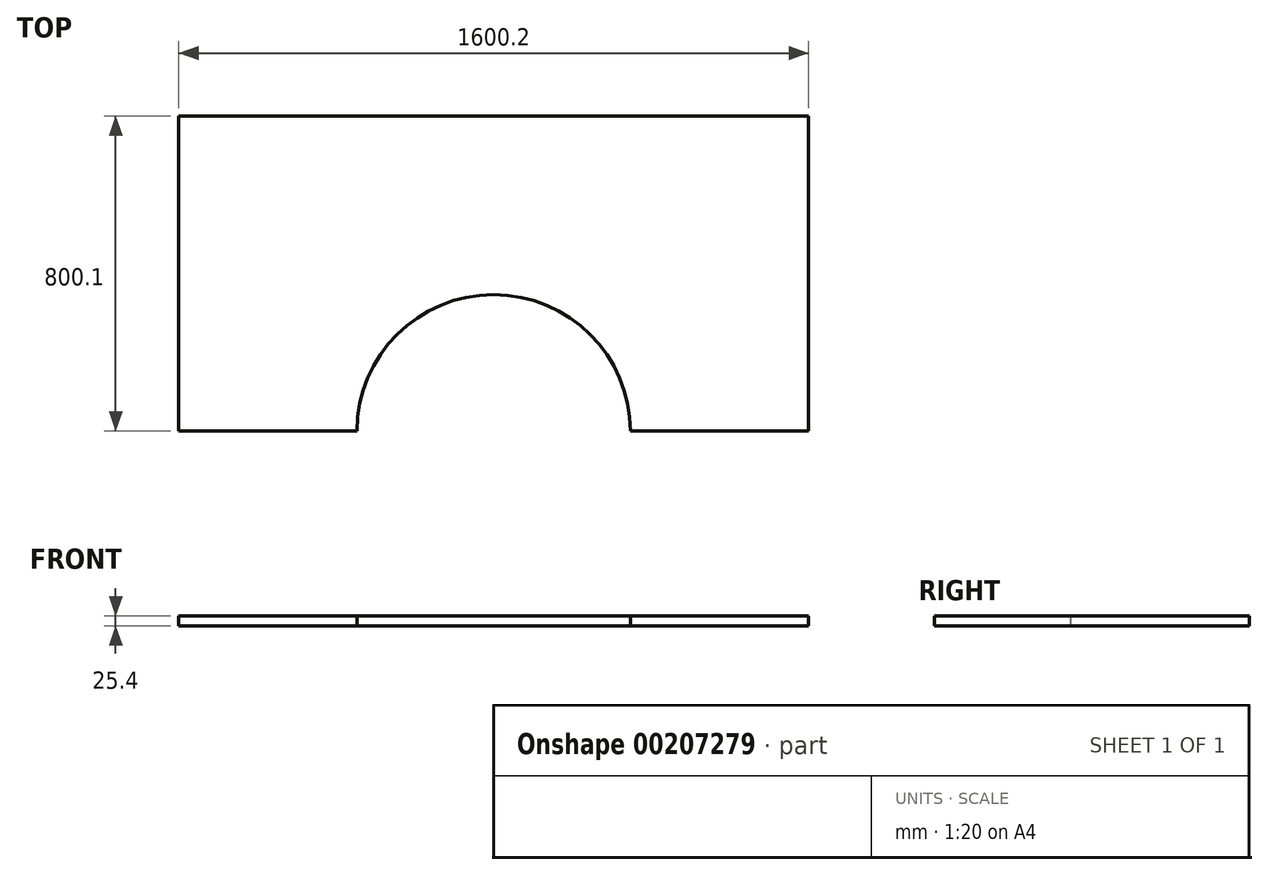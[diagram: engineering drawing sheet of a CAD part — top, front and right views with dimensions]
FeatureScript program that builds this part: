
annotation { "Feature Type Name" : "Feature", "Feature Type Description" : "" }
export const myFeature = defineFeature(function(context is Context, id is Id, definition is map)
    precondition{}
    {
        {
            var Q0;
            Q0=qCreatedBy(makeId("Top.planeOp"),FACE);
            var sketch = newSketch(context, id + "F0", { "sketchPlane" : qUnion([Q0])});
            skLineSegment(sketch, "E0.bottom", {"start": v(-800.1, -400.05) * mm, "end": v(800.1, -400.05) * mm});
            skLineSegment(sketch, "E0.top", {"start": v(-800.1, 400.05) * mm, "end": v(800.1, 400.05) * mm});
            skLineSegment(sketch, "E0.left", {"start": v(-800.1, -400.05) * mm, "end": v(-800.1, 400.05) * mm});
            skLineSegment(sketch, "E0.right", {"start": v(800.1, -400.05) * mm, "end": v(800.1, 400.05) * mm});
            skPoint(sketch, "E0.middle", {"position": v(0, 0) * mm});
            skSolve(sketch);
        }
        {
            var Q0;
            Q0=makeQuery(id+"F0.imprint","IMPRINT",FACE,{"disambiguationData":[TD([[makeQuery(id+"F0.imprint","IMPRINT",EDGE,{"derivedFrom":sQuery(id+"F0.wireOp",EDGE,"E0.bottom")}),1.0]])]});
            extrude(context, id + "F1", {"entities" : qUnion([Q0]), "depth" : 25.4 * mm});
        }
        {
            var Q0;
            Q0=qCreatedBy(makeId("Top.planeOp"),FACE);
            var sketch = newSketch(context, id + "F2", { "sketchPlane" : qUnion([Q0])});
            skArc(sketch, "E1", {"start": v(347.4, -401.08) * mm, "mid": v(0, -53.69) * mm, "end": v(-347.4, -401.08) * mm});
            skLineSegment(sketch, "E2", {"start": v(-347.4, -401.08) * mm, "end": v(347.4, -401.08) * mm});
            skSolve(sketch);
        }
        {
            var Q0;
            Q0 = qSketchRegion(id + "F2", true);
            extrude(context, id + "F3", {"entities" : qUnion([Q0]), "operationType" : NewBodyOperationType.REMOVE, "endBound" : BoundingType.SYMMETRIC, "oppositeDirection" : true, "depth" : 50.8 * mm});
        }
    });
